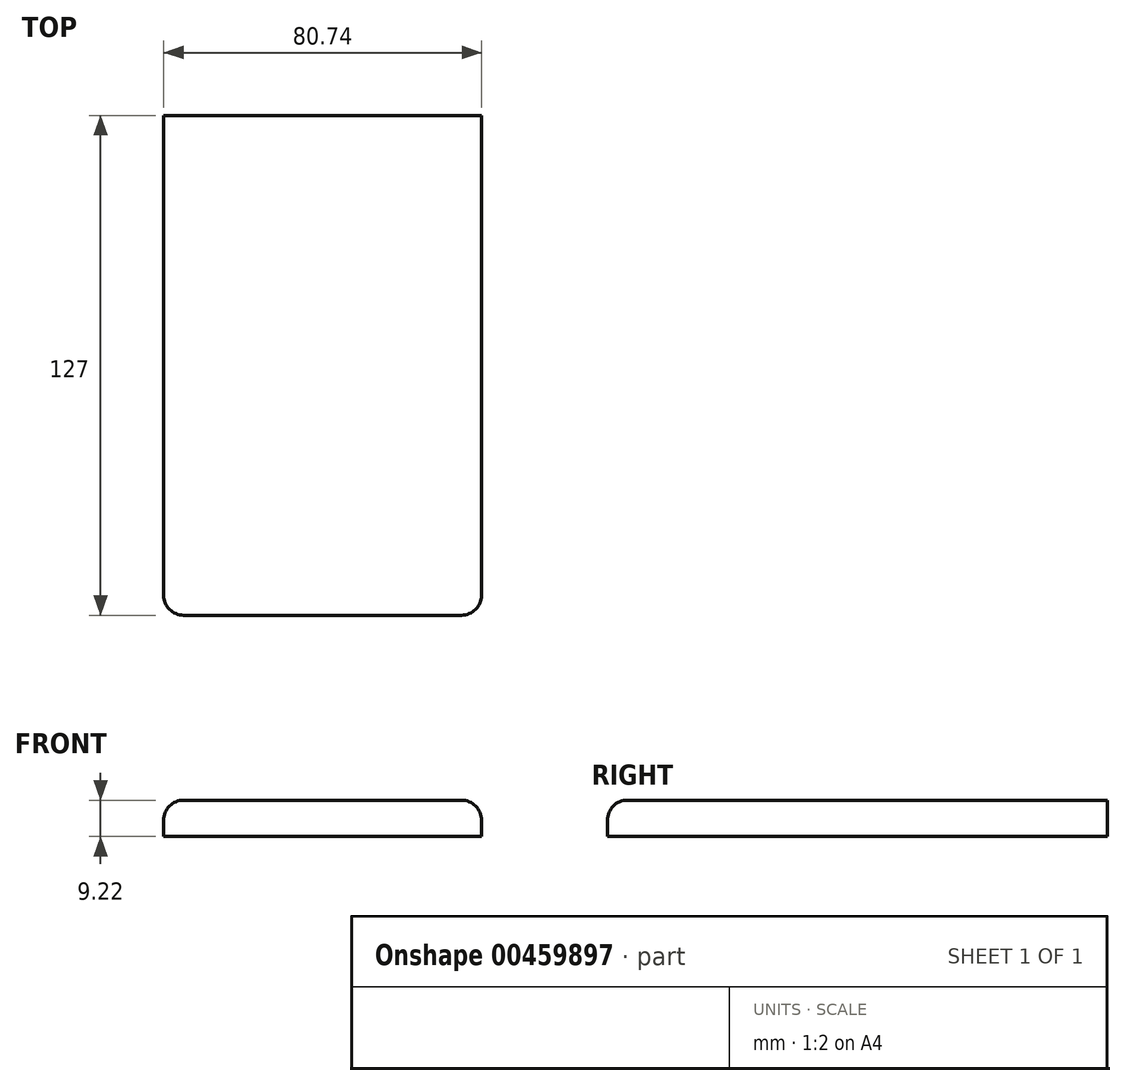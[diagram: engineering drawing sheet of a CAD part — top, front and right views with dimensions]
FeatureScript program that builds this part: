
annotation { "Feature Type Name" : "Feature", "Feature Type Description" : "" }
export const myFeature = defineFeature(function(context is Context, id is Id, definition is map)
    precondition{}
    {
        {
            var Q0;
            Q0=qCreatedBy(makeId("Front.planeOp"),FACE);
            var sketch = newSketch(context, id + "F0", { "sketchPlane" : qUnion([Q0])});
            skLineSegment(sketch, "E0.bottom", {"start": v(-40.37, 4.6) * mm, "end": v(40.37, 4.6) * mm});
            skLineSegment(sketch, "E0.top", {"start": v(-40.37, -4.6) * mm, "end": v(40.37, -4.6) * mm});
            skLineSegment(sketch, "E0.left", {"start": v(-40.37, 4.6) * mm, "end": v(-40.37, -4.6) * mm});
            skLineSegment(sketch, "E0.right", {"start": v(40.37, 4.6) * mm, "end": v(40.37, -4.6) * mm});
            skPoint(sketch, "E0.middle", {"position": v(0, 0) * mm});
            skSolve(sketch);
        }
        {
            var Q0;
            Q0=makeQuery(id+"F0.imprint","IMPRINT",FACE,{"disambiguationData":[TD([[makeQuery(id+"F0.imprint","IMPRINT",EDGE,{"derivedFrom":sQuery(id+"F0.wireOp",EDGE,"E0.bottom")}),-1.0]])]});
            extrude(context, id + "F1", {"entities" : qUnion([Q0]), "depth" : 127 * mm});
        }
        {
            var Q0;
            Q0=makeQuery(id+"F1.opExtrude","CAP_EDGE",EDGE,{"disambiguationData":[OSD([sQuery(id+"F0.wireOp",EDGE,"E0.bottom")])],"isStart":false});
            fillet(context, id + "F2", {"entities" : qUnion([Q0]), "radius" : 5.08 * mm, "tangentPropagation" : true, "allowEdgeOverflow" : false});
        }
        {
            var Q0;
            Q0=makeQuery(id+"F1.opExtrude","SWEPT_EDGE",EDGE,{"disambiguationData":[OSD([sQuery(id+"F0.wireOp",EDGE,"E0.bottom"),sQuery(id+"F0.wireOp",EDGE,"E0.right")])]});
            fillet(context, id + "F3", {"entities" : qUnion([Q0]), "radius" : 5.08 * mm, "tangentPropagation" : true, "allowEdgeOverflow" : false});
        }
        {
            var Q0;
            Q0=makeQuery(id+"F1.opExtrude","SWEPT_EDGE",EDGE,{"disambiguationData":[OSD([sQuery(id+"F0.wireOp",EDGE,"E0.bottom"),sQuery(id+"F0.wireOp",EDGE,"E0.left")])]});
            fillet(context, id + "F4", {"entities" : qUnion([Q0]), "radius" : 5.08 * mm, "tangentPropagation" : true, "allowEdgeOverflow" : false});
        }
    });
